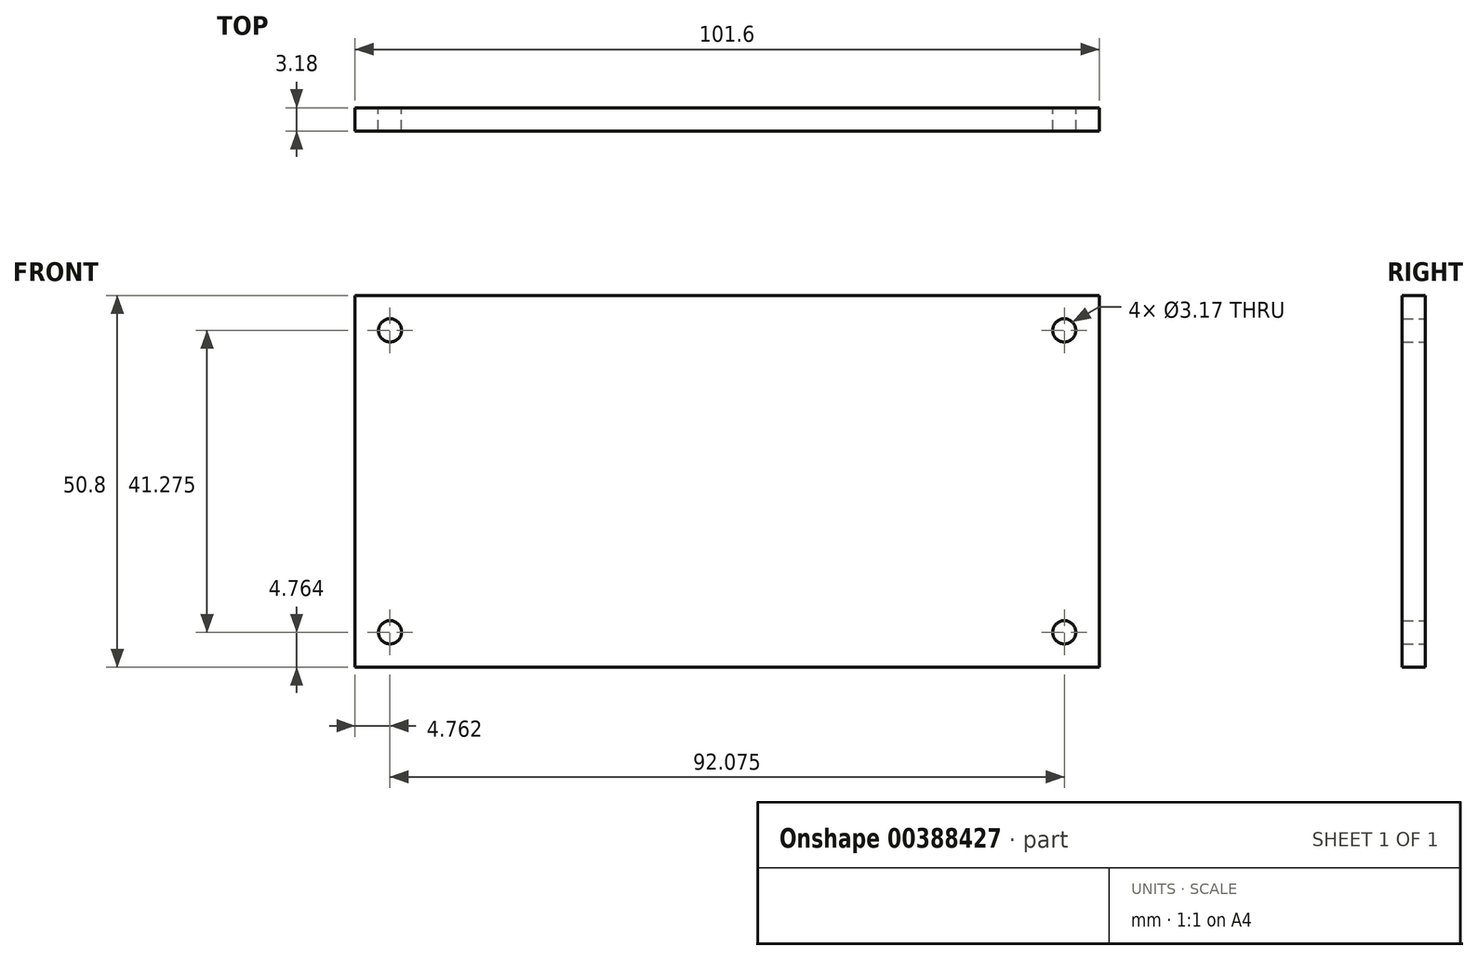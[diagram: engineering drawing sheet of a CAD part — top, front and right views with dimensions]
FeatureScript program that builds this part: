
annotation { "Feature Type Name" : "Feature", "Feature Type Description" : "" }
export const myFeature = defineFeature(function(context is Context, id is Id, definition is map)
    precondition{}
    {
        {
            var Q0;
            Q0=qCreatedBy(makeId("Front.planeOp"),FACE);
            var sketch = newSketch(context, id + "F0", { "sketchPlane" : qUnion([Q0])});
            skLineSegment(sketch, "E0.bottom", {"start": v(-33.8, 10.63) * mm, "end": v(67.8, 10.63) * mm});
            skLineSegment(sketch, "E0.top", {"start": v(-33.8, -40.17) * mm, "end": v(67.8, -40.17) * mm});
            skLineSegment(sketch, "E0.left", {"start": v(-33.8, 10.63) * mm, "end": v(-33.8, -40.17) * mm});
            skLineSegment(sketch, "E0.right", {"start": v(67.8, 10.63) * mm, "end": v(67.8, -40.17) * mm});
            skSolve(sketch);
        }
        {
            var Q0;
            Q0=makeQuery(id+"F0.imprint","IMPRINT",FACE,{"disambiguationData":[TD([[makeQuery(id+"F0.imprint","IMPRINT",EDGE,{"derivedFrom":sQuery(id+"F0.wireOp",EDGE,"E0.bottom")}),-1.0]])]});
            extrude(context, id + "F1", {"entities" : qUnion([Q0]), "depth" : 3.17 * mm});
        }
        {
            var Q0;
            Q0=makeQuery(id+"F1.opExtrude","CAP_FACE",FACE,{"disambiguationData":[OSD([sQuery(id+"F0.wireOp",EDGE,"E0.bottom"),sQuery(id+"F0.wireOp",EDGE,"E0.top"),sQuery(id+"F0.wireOp",EDGE,"E0.left"),sQuery(id+"F0.wireOp",EDGE,"E0.right")])],"isStart":true});
            var sketch = newSketch(context, id + "F2", { "sketchPlane" : qUnion([Q0])});
            skCircle(sketch, "E1", {"center": v(-63.04, 5.87) * mm, "radius": 1.59 * mm});
            skCircle(sketch, "E2", {"center": v(-63.04, -35.4) * mm, "radius": 1.59 * mm});
            skCircle(sketch, "E3", {"center": v(29.04, 5.87) * mm, "radius": 1.59 * mm});
            skCircle(sketch, "E4", {"center": v(29.04, -35.4) * mm, "radius": 1.59 * mm});
            skSolve(sketch);
        }
        {
            var Q0;
            Q0 = qSketchRegion(id + "F2", true);
            extrude(context, id + "F3", {"entities" : qUnion([Q0]), "operationType" : NewBodyOperationType.REMOVE, "oppositeDirection" : true, "depth" : 25.4 * mm});
        }
        {
            var Q0;
            Q0=makeQuery(id+"F1.opExtrude","CAP_FACE",FACE,{"disambiguationData":[OSD([sQuery(id+"F0.wireOp",EDGE,"E0.bottom"),sQuery(id+"F0.wireOp",EDGE,"E0.top"),sQuery(id+"F0.wireOp",EDGE,"E0.left"),sQuery(id+"F0.wireOp",EDGE,"E0.right")])],"isStart":false});
            var sketch = newSketch(context, id + "F4", { "sketchPlane" : qUnion([Q0])});
            skLineSegment(sketch, "E5.bottom", {"start": v(0, -32.86) * mm, "end": v(50.8, -32.86) * mm});
            skLineSegment(sketch, "E5.top", {"start": v(0, -7.46) * mm, "end": v(50.8, -7.46) * mm});
            skLineSegment(sketch, "E5.left", {"start": v(0, -32.86) * mm, "end": v(0, -7.46) * mm});
            skLineSegment(sketch, "E5.right", {"start": v(50.8, -32.86) * mm, "end": v(50.8, -7.46) * mm});
            skCircle(sketch, "E6", {"center": v(25.4, -20.16) * mm, "radius": 3.18 * mm});
            skSolve(sketch);
        }
        {
            var Q0;
            Q0=makeQuery(id+"F4.imprint","IMPRINT",FACE,{"disambiguationData":[TD([[makeQuery(id+"F4.imprint","IMPRINT",EDGE,{"derivedFrom":sQuery(id+"F4.wireOp",EDGE,"E6")}),1.0]])]});
            extrude(context, id + "F5", {"entities" : qUnion([Q0]), "operationType" : NewBodyOperationType.REMOVE, "depth" : 25.4 * mm});
        }
    });
